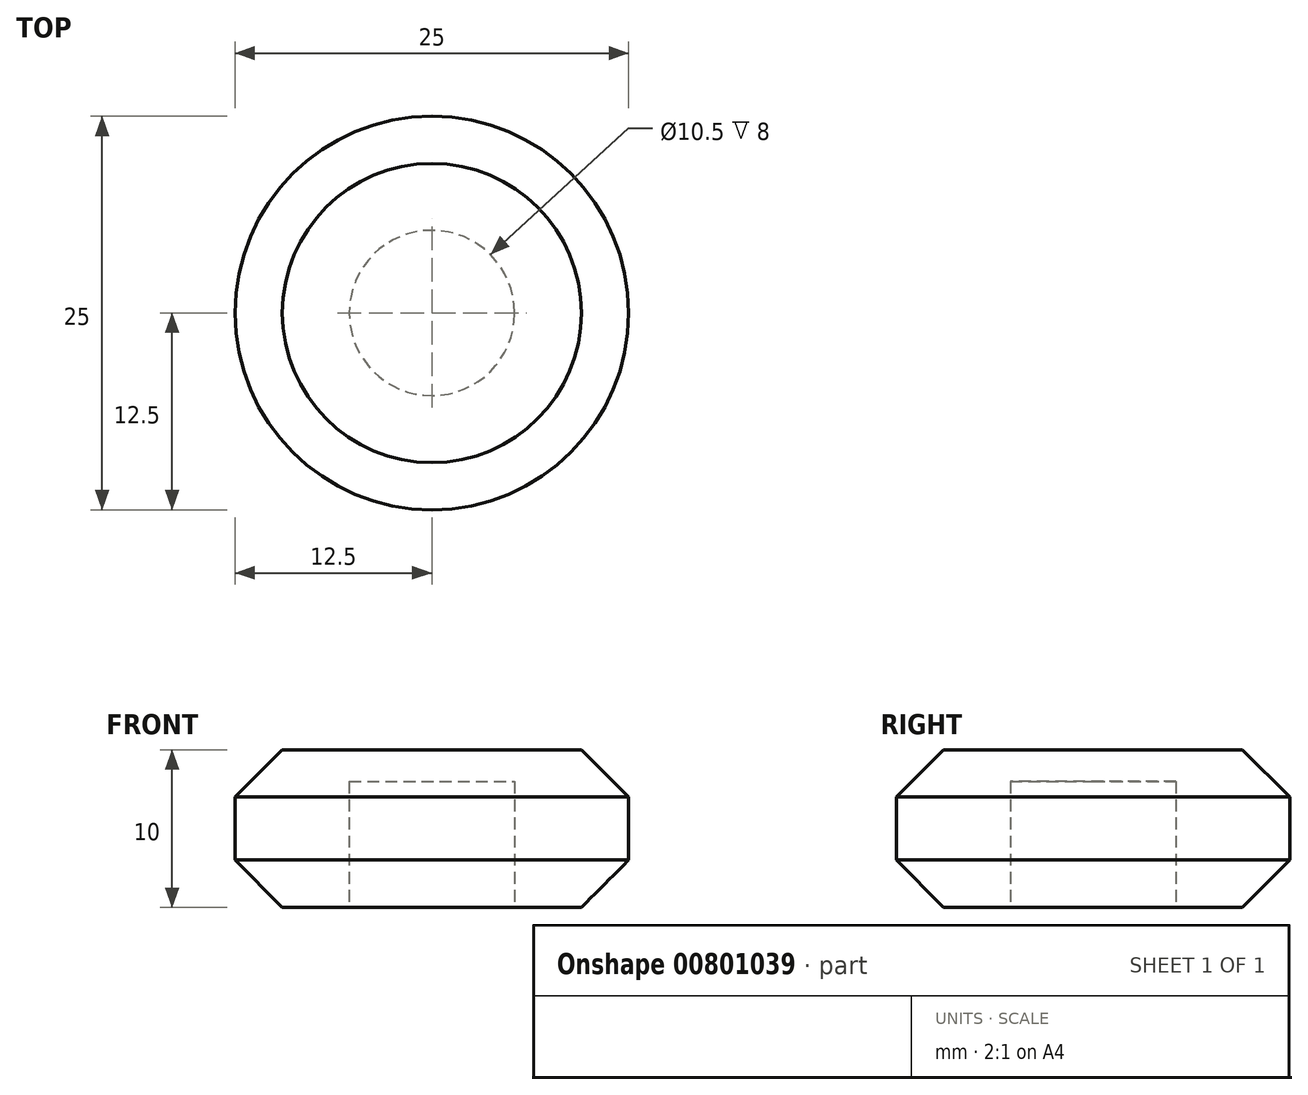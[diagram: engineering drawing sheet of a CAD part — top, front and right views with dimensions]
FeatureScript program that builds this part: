
annotation { "Feature Type Name" : "Feature", "Feature Type Description" : "" }
export const myFeature = defineFeature(function(context is Context, id is Id, definition is map)
    precondition{}
    {
        {
            var Q0;
            Q0=qCreatedBy(makeId("Top.planeOp"),FACE);
            var sketch = newSketch(context, id + "F0", { "sketchPlane" : qUnion([Q0])});
            skCircle(sketch, "E0", {"center": v(0, 0) * mm, "radius": 12.5 * mm});
            skSolve(sketch);
        }
        {
            var Q0;
            Q0=makeQuery(id+"F0.imprint","IMPRINT",FACE,{"disambiguationData":[TD([[makeQuery(id+"F0.imprint","IMPRINT",EDGE,{"derivedFrom":sQuery(id+"F0.wireOp",EDGE,"lb8Q771R-3qZJ-0uqt-ry7f-P8V1LYdMRFgS")}),-1.0]])]});
            var Q1;
            Q1=makeQuery(id+"F0.imprint","IMPRINT",FACE,{"disambiguationData":[TD([[makeQuery(id+"F0.imprint","IMPRINT",EDGE,{"derivedFrom":sQuery(id+"F0.wireOp",EDGE,"E0")}),1.0]])]});
            extrude(context, id + "F1", {"entities" : qUnion([Q0, Q1]), "depth" : 10 * mm, "offsetDistance" : 25 * mm});
        }
        {
            var Q0;
            Q0=makeQuery(id+"F1.opExtrude","CAP_EDGE",EDGE,{"disambiguationData":[OSD([sQuery(id+"F0.wireOp",EDGE,"E0")])],"isStart":false});
            var Q1;
            Q1=makeQuery(id+"F1.opExtrude","SWEPT_FACE",FACE,{"disambiguationData":[OSD([sQuery(id+"F0.wireOp",EDGE,"E0")])]});
            chamfer(context, id + "F2", {"entities" : qUnion([Q0, Q1]), "width" : 3 * mm, "tangentPropagation" : true});
        }
        {
            var Q0;
            Q0=makeQuery(id+"F1.opExtrude","CAP_FACE",FACE,{"disambiguationData":[OSD([sQuery(id+"F0.wireOp",EDGE,"E0")])],"isStart":true});
            var sketch = newSketch(context, id + "F3", { "sketchPlane" : qUnion([Q0])});
            skPoint(sketch, "E1", {"position": v(0, 0) * mm});
            skCircle(sketch, "E2", {"center": v(0, 0) * mm, "radius": 5.25 * mm});
            skSolve(sketch);
        }
        {
            var Q0;
            Q0=makeQuery(id+"F3.imprint","IMPRINT",FACE,{"disambiguationData":[TD([[makeQuery(id+"F3.imprint","IMPRINT",EDGE,{"derivedFrom":sQuery(id+"F3.wireOp",EDGE,"E2")}),1.0]])]});
            extrude(context, id + "F4", {"entities" : qUnion([Q0]), "operationType" : NewBodyOperationType.REMOVE, "oppositeDirection" : true, "depth" : 8 * mm, "offsetDistance" : 25 * mm});
        }
    });
